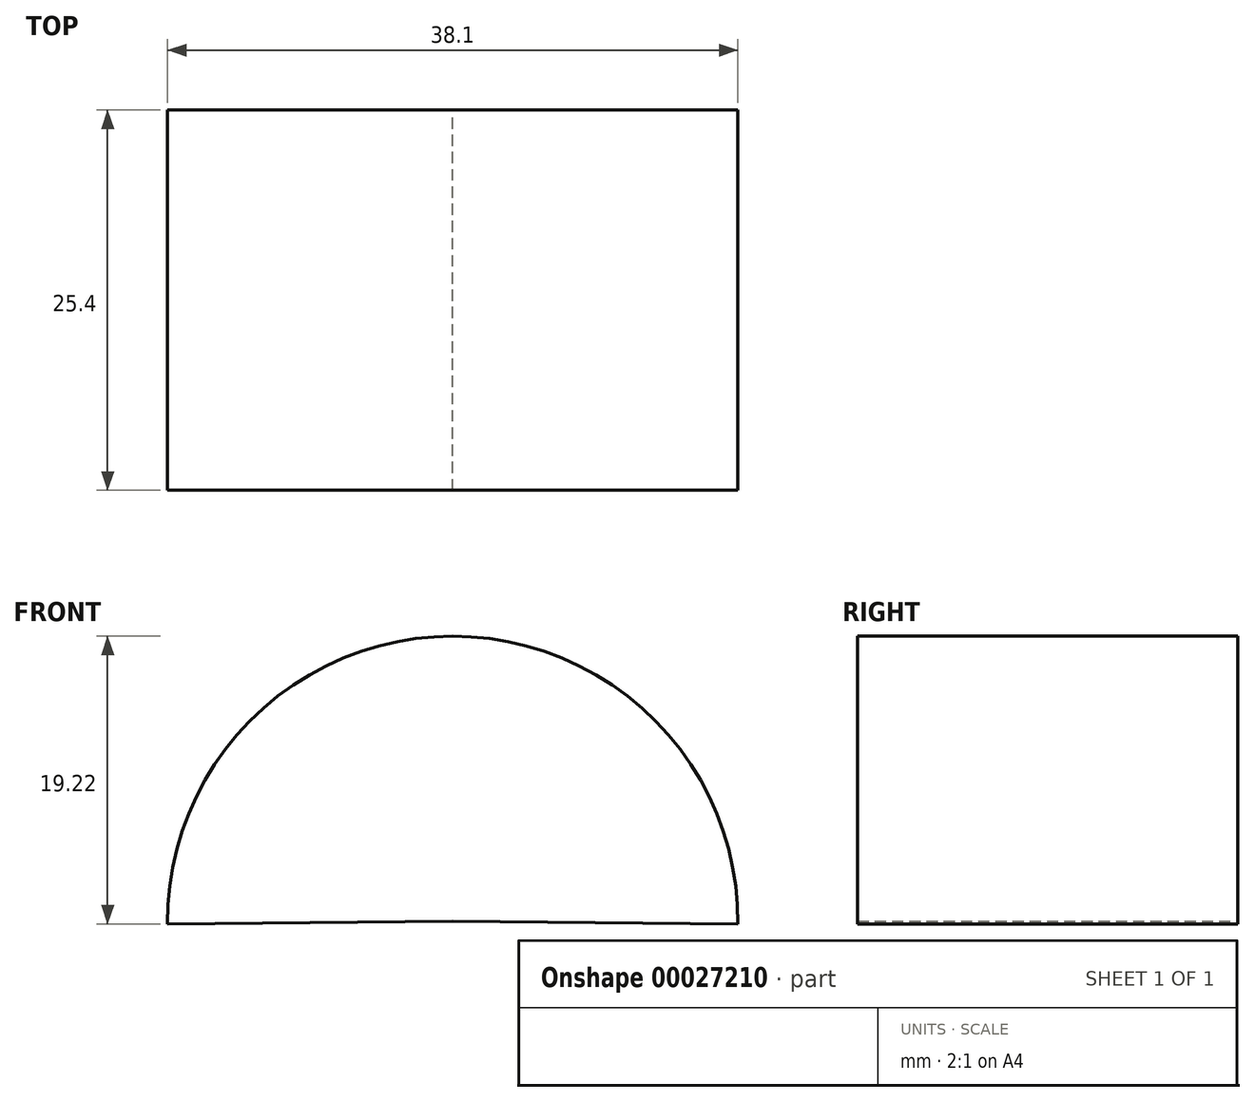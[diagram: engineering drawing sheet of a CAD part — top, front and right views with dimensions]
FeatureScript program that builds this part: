
annotation { "Feature Type Name" : "Feature", "Feature Type Description" : "" }
export const myFeature = defineFeature(function(context is Context, id is Id, definition is map)
    precondition{}
    {
        {
            var Q0;
            Q0=qCreatedBy(makeId("Front.planeOp"),FACE);
            var sketch = newSketch(context, id + "F0", { "sketchPlane" : qUnion([Q0])});
            skArc(sketch, "E0", {"start": v(38.1, 0) * mm, "mid": v(19.05, 19.22) * mm, "end": v(0, 0) * mm});
            skLineSegment(sketch, "E1", {"start": v(0, 0) * mm, "end": v(19.05, 0.17) * mm});
            skLineSegment(sketch, "E2", {"start": v(38.1, 0) * mm, "end": v(19.05, 0.17) * mm});
            skSolve(sketch);
        }
        {
            var Q0;
            Q0=makeQuery(id+"F0.imprint","IMPRINT",FACE,{"disambiguationData":[TD([[makeQuery(id+"F0.imprint","IMPRINT",EDGE,{"derivedFrom":sQuery(id+"F0.wireOp",EDGE,"E0")}),1.0]])]});
            extrude(context, id + "F1", {"entities" : qUnion([Q0]), "depth" : 25.4 * mm});
        }
    });
